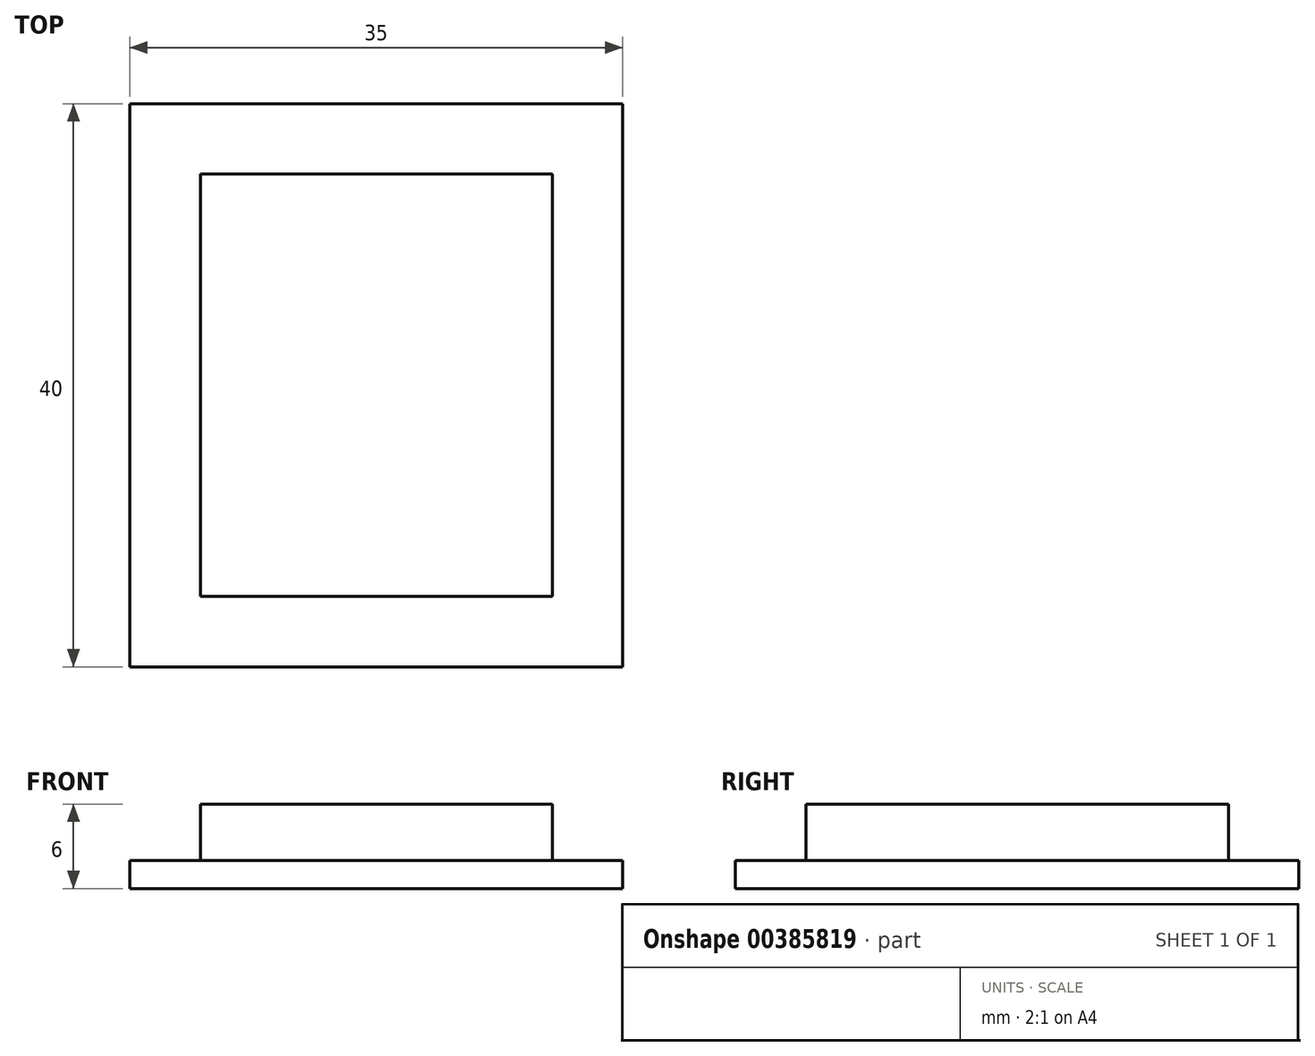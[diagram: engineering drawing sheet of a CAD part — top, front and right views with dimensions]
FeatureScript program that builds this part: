
annotation { "Feature Type Name" : "Feature", "Feature Type Description" : "" }
export const myFeature = defineFeature(function(context is Context, id is Id, definition is map)
    precondition{}
    {
        {
            var Q0;
            Q0=qCreatedBy(makeId("Top.planeOp"),FACE);
            var sketch = newSketch(context, id + "F0", { "sketchPlane" : qUnion([Q0])});
            skLineSegment(sketch, "E0.0", {"start": v(45.5, 5.5) * mm, "end": v(45.5, 45.5) * mm});
            skLineSegment(sketch, "E0.1", {"start": v(10.5, 5.5) * mm, "end": v(45.5, 5.5) * mm});
            skLineSegment(sketch, "E0.2", {"start": v(10.5, 5.5) * mm, "end": v(10.5, 45.5) * mm});
            skLineSegment(sketch, "E0.3", {"start": v(10.5, 45.5) * mm, "end": v(45.5, 45.5) * mm});
            skSolve(sketch);
        }
        {
            var Q0;
            Q0=qSketchRegion(id+"F0",true);
            extrude(context, id + "F1", {"entities" : qUnion([Q0]), "depth" : 2 * mm});
        }
        {
            var Q0;
            Q0=makeQuery(id+"F1.opExtrude","CAP_FACE",FACE,{"disambiguationData":[OSD([sQuery(id+"F0.wireOp",EDGE,"92cctflQ-2F0k-CWzI-Jkwk-uNcrXzVTXhU9.bottom"),sQuery(id+"F0.wireOp",EDGE,"92cctflQ-2F0k-CWzI-Jkwk-uNcrXzVTXhU9.top"),sQuery(id+"F0.wireOp",EDGE,"92cctflQ-2F0k-CWzI-Jkwk-uNcrXzVTXhU9.left"),sQuery(id+"F0.wireOp",EDGE,"92cctflQ-2F0k-CWzI-Jkwk-uNcrXzVTXhU9.right"),sQuery(id+"F0.wireOp",EDGE,"E0.0"),sQuery(id+"F0.wireOp",EDGE,"E0.1"),sQuery(id+"F0.wireOp",EDGE,"E0.2"),sQuery(id+"F0.wireOp",EDGE,"E0.3")])],"isStart":false});
            var sketch = newSketch(context, id + "F2", { "sketchPlane" : qUnion([Q0])});
            skLineSegment(sketch, "E1.0", {"start": v(15.5, 40.5) * mm, "end": v(40.5, 40.5) * mm});
            skLineSegment(sketch, "E1.1", {"start": v(15.5, 10.5) * mm, "end": v(15.5, 40.5) * mm});
            skLineSegment(sketch, "E1.2", {"start": v(15.5, 10.5) * mm, "end": v(40.5, 10.5) * mm});
            skLineSegment(sketch, "E1.3", {"start": v(40.5, 10.5) * mm, "end": v(40.5, 40.5) * mm});
            skSolve(sketch);
        }
        {
            var Q0;
            Q0=qSketchRegion(id+"F2",true);
            extrude(context, id + "F3", {"entities" : qUnion([Q0]), "operationType" : NewBodyOperationType.ADD, "depth" : 4 * mm});
        }
    });
